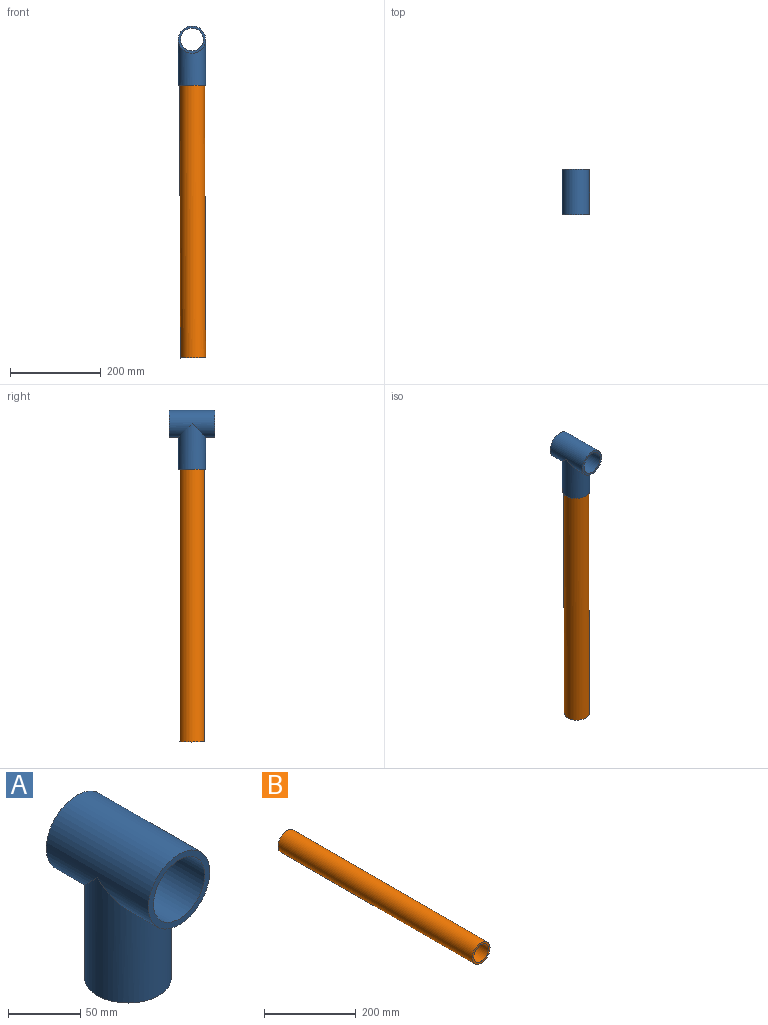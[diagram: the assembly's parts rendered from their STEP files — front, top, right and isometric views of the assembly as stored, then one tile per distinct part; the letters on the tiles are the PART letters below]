
ASSEMBLY  parts=2 mates=1
PART A: 8 faces, bbox 60x100x130 mm
  f0: cylinder r=30mm len=100mm, axis (0,1,0), area 15249.6mm2, adj f2,f3,f5
  f1: cylinder r=25mm len=100mm, axis (0,1,0), area 15708mm2, adj f2,f3
  f2: plane 60x60mm, normal (0,-1,0), area 863.9mm2, adj f0,f1
  f3: plane 60x60mm, normal (0,1,0), area 863.9mm2, adj f0,f1
  f4: plane 60x60mm, normal (0,0,-1), area 863.9mm2, adj f5,f6
  f5: cylinder r=30mm len=100mm, axis (0,0,-1), area 15249.6mm2, adj f0,f4
  f6: cylinder r=25mm len=83.42mm, axis (0,0,-1), area 11971.6mm2, adj f4,f7
  f7: cylinder r=30mm len=50mm, axis (0,1,0), area 2208.5mm2, adj f6
PART B: 4 faces, bbox 55x600x55 mm
  f0: cylinder r=22.5mm len=600mm, axis (0,1,0), area 84823mm2, adj f2,f3
  f1: cylinder r=27.5mm len=600mm, axis (0,1,0), area 103672.6mm2, adj f2,f3
  f2: plane 55x55mm, normal (0,-1,0), area 785.4mm2, adj f0,f1
  f3: plane 55x55mm, normal (0,1,0), area 785.4mm2, adj f0,f1
PLACE A rot(axis=(0,-1,0),0.2deg) t=(8.85,-106.72,13.2)mm
PLACE B rot(axis=(-1,0,0),90deg) t=(11.48,-106.72,-686.79)mm
MATE fastened B.f1 <-> A.f5  axis (0,0,1) through (9.22,-106.72,-86.8)mm
